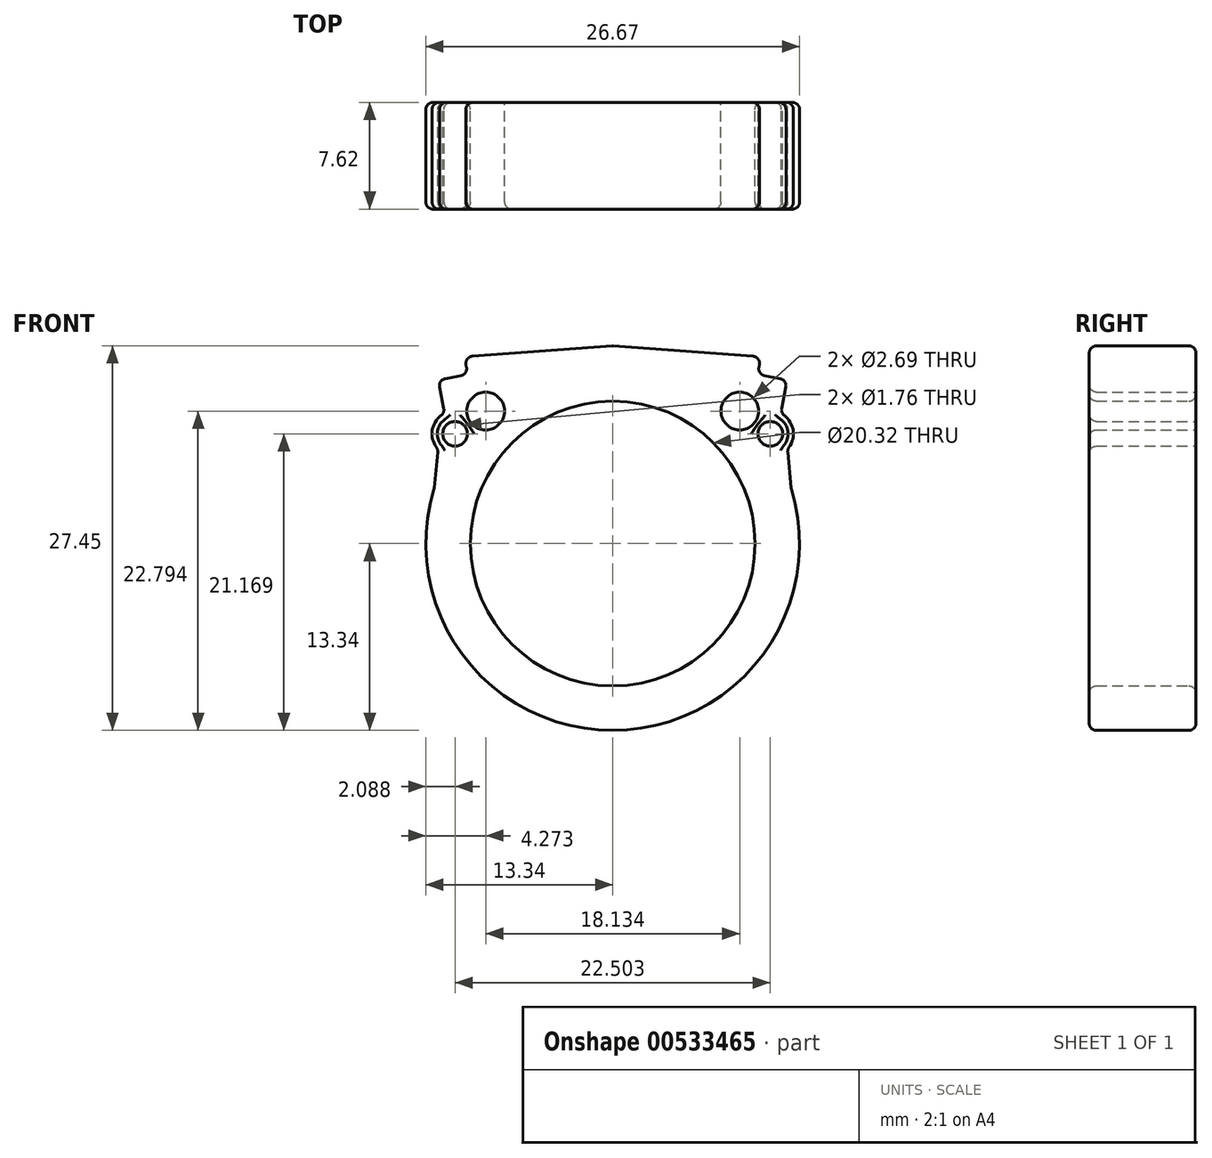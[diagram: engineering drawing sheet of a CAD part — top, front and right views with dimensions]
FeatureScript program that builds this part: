
annotation { "Feature Type Name" : "Feature", "Feature Type Description" : "" }
export const myFeature = defineFeature(function(context is Context, id is Id, definition is map)
    precondition{}
    {
        {
            var Q0;
            Q0=qCreatedBy(makeId("Front.planeOp"),FACE);
            var sketch = newSketch(context, id + "F0", { "sketchPlane" : qUnion([Q0])});
            skCircle(sketch, "E0", {"center": v(0, 0) * mm, "radius": 10.16 * mm});
            skArc(sketch, "E1.0", {"start": v(-12.74, 3.94) * mm, "mid": v(0, -13.34) * mm, "end": v(12.74, 3.94) * mm});
            skLineSegment(sketch, "E2", {"start": v(-11.99, 9.3) * mm, "end": v(-12.45, 11.66) * mm});
            skLineSegment(sketch, "E3", {"start": v(-12.45, 11.66) * mm, "end": v(-10.34, 12.08) * mm});
            skPoint(sketch, "E4.orphan", {"position": v(-10.16, 0) * mm});
            skArc(sketch, "E5", {"start": v(-11.99, 9.3) * mm, "mid": v(-12.88, 8.06) * mm, "end": v(-12.36, 6.62) * mm});
            skLineSegment(sketch, "E6", {"start": v(-10.34, 12.08) * mm, "end": v(-10.58, 13.32) * mm});
            skLineSegment(sketch, "E7", {"start": v(-10.58, 13.32) * mm, "end": v(0, 14.11) * mm});
            skLineSegment(sketch, "E8.MirrorCS", {"start": v(12.5, 6.46) * mm, "end": v(12.36, 6.62) * mm});
            skLineSegment(sketch, "E9.MirrorCS", {"start": v(10.58, 13.32) * mm, "end": v(0, 14.11) * mm});
            skLineSegment(sketch, "E10.MirrorCS", {"start": v(10.34, 12.08) * mm, "end": v(10.58, 13.32) * mm});
            skLineSegment(sketch, "E11.MirrorCS", {"start": v(12.45, 11.66) * mm, "end": v(10.34, 12.08) * mm});
            skArc(sketch, "E12.MirrorCS", {"start": v(11.99, 9.3) * mm, "mid": v(12.88, 8.06) * mm, "end": v(12.36, 6.62) * mm});
            skLineSegment(sketch, "E13.MirrorCS", {"start": v(11.99, 9.3) * mm, "end": v(12.45, 11.66) * mm});
            skPoint(sketch, "E14.start.orphan", {"position": v(-13.37, 5.42) * mm});
            skLineSegment(sketch, "E15", {"start": v(-12.74, 3.94) * mm, "end": v(-12.47, 6.73) * mm});
            skPoint(sketch, "E16.orphan", {"position": v(-12.36, 7.86) * mm});
            skLineSegment(sketch, "E17.MirrorCS", {"start": v(12.74, 3.94) * mm, "end": v(12.47, 6.73) * mm});
            skPoint(sketch, "E18.MirrorCS.end.orphan", {"position": v(13.37, 5.42) * mm});
            skPoint(sketch, "E18.MirrorCS.start.orphan", {"position": v(12.74, 3.94) * mm});
            skSolve(sketch);
        }
        {
            var Q0;
            Q0 = qSketchRegion(id + "F0", true);
            extrude(context, id + "F1", {"entities" : qUnion([Q0]), "depth" : 7.62 * mm, "offsetDistance" : 25.4 * mm});
        }
        {
            var Q0;
            Q0=makeQuery(id+"F1.opExtrude","CAP_FACE",FACE,{"disambiguationData":[OSD([sQuery(id+"F0.wireOp",EDGE,"E0"),sQuery(id+"F0.wireOp",EDGE,"E1.0"),sQuery(id+"F0.wireOp",EDGE,"E2"),sQuery(id+"F0.wireOp",EDGE,"E3"),sQuery(id+"F0.wireOp",EDGE,"E5"),sQuery(id+"F0.wireOp",EDGE,"E6"),sQuery(id+"F0.wireOp",EDGE,"E7"),sQuery(id+"F0.wireOp",EDGE,"E9.MirrorCS"),sQuery(id+"F0.wireOp",EDGE,"E10.MirrorCS"),sQuery(id+"F0.wireOp",EDGE,"E11.MirrorCS"),sQuery(id+"F0.wireOp",EDGE,"E12.MirrorCS"),sQuery(id+"F0.wireOp",EDGE,"E13.MirrorCS"),sQuery(id+"F0.wireOp",EDGE,"E15"),sQuery(id+"F0.wireOp",EDGE,"E17.MirrorCS")])],"isStart":true});
            var sketch = newSketch(context, id + "F2", { "sketchPlane" : qUnion([Q0])});
            skCircle(sketch, "E19", {"center": v(-9.07, 9.45) * mm, "radius": 1.34 * mm});
            skCircle(sketch, "E20", {"center": v(-11.25, 7.83) * mm, "radius": 0.88 * mm});
            skCircle(sketch, "E21.MirrorC", {"center": v(9.07, 9.45) * mm, "radius": 1.34 * mm});
            skCircle(sketch, "E22.MirrorC", {"center": v(11.25, 7.83) * mm, "radius": 0.88 * mm});
            skSolve(sketch);
        }
        {
            var Q0;
            Q0 = qSketchRegion(id + "F2", true);
            extrude(context, id + "F3", {"entities" : qUnion([Q0]), "operationType" : NewBodyOperationType.REMOVE, "endBound" : BoundingType.THROUGH_ALL, "oppositeDirection" : true, "depth" : 25.4 * mm, "offsetDistance" : 25.4 * mm});
        }
        {
            var Q0;
            Q0=makeQuery(id+"F1.opExtrude","CAP_EDGE",EDGE,{"disambiguationData":[OSD([sQuery(id+"F0.wireOp",EDGE,"E0")])],"isStart":false});
            var Q1;
            Q1=makeQuery(id+"F1.opExtrude","SWEPT_EDGE",EDGE,{"disambiguationData":[OSD([sQuery(id+"F0.wireOp",EDGE,"E1.0"),sQuery(id+"F0.wireOp",EDGE,"E17.MirrorCS")])]});
            var Q2;
            Q2=makeQuery(id+"F1.opExtrude","CAP_EDGE",EDGE,{"disambiguationData":[OSD([sQuery(id+"F0.wireOp",EDGE,"E1.0")])],"isStart":true});
            var Q3;
            Q3=makeQuery(id+"F1.opExtrude","SWEPT_EDGE",EDGE,{"disambiguationData":[OSD([sQuery(id+"F0.wireOp",EDGE,"E10.MirrorCS"),sQuery(id+"F0.wireOp",EDGE,"E11.MirrorCS")])]});
            var Q4;
            Q4=makeQuery(id+"F1.opExtrude","SWEPT_EDGE",EDGE,{"disambiguationData":[OSD([sQuery(id+"F0.wireOp",EDGE,"E9.MirrorCS"),sQuery(id+"F0.wireOp",EDGE,"E10.MirrorCS")])]});
            var Q5;
            Q5=makeQuery(id+"F1.opExtrude","SWEPT_EDGE",EDGE,{"disambiguationData":[OSD([sQuery(id+"F0.wireOp",EDGE,"E12.MirrorCS"),sQuery(id+"F0.wireOp",EDGE,"E13.MirrorCS")])]});
            var Q6;
            Q6=makeQuery(id+"F1.opExtrude","CAP_EDGE",EDGE,{"disambiguationData":[OSD([sQuery(id+"F0.wireOp",EDGE,"E9.MirrorCS")])],"isStart":false});
            var Q7;
            Q7=makeQuery(id+"F1.opExtrude","SWEPT_EDGE",EDGE,{"disambiguationData":[OSD([sQuery(id+"F0.wireOp",EDGE,"E11.MirrorCS"),sQuery(id+"F0.wireOp",EDGE,"E13.MirrorCS")])]});
            var Q8;
            Q8=makeQuery(id+"F1.opExtrude","CAP_EDGE",EDGE,{"disambiguationData":[OSD([sQuery(id+"F0.wireOp",EDGE,"E12.MirrorCS")])],"isStart":true});
            var Q9;
            Q9=makeQuery(id+"F1.opExtrude","CAP_EDGE",EDGE,{"disambiguationData":[OSD([sQuery(id+"F0.wireOp",EDGE,"E1.0")])],"isStart":false});
            var Q10;
            Q10=makeQuery(id+"F1.opExtrude","SWEPT_EDGE",EDGE,{"disambiguationData":[OSD([sQuery(id+"F0.wireOp",EDGE,"E12.MirrorCS"),sQuery(id+"F0.wireOp",EDGE,"E17.MirrorCS")])]});
            var Q11;
            Q11=makeQuery(id+"F1.opExtrude","CAP_EDGE",EDGE,{"disambiguationData":[OSD([sQuery(id+"F0.wireOp",EDGE,"E12.MirrorCS")])],"isStart":false});
            var Q12;
            Q12=makeQuery(id+"F1.opExtrude","CAP_EDGE",EDGE,{"disambiguationData":[OSD([sQuery(id+"F0.wireOp",EDGE,"E10.MirrorCS")])],"isStart":false});
            var Q13;
            Q13=makeQuery(id+"F1.opExtrude","SWEPT_EDGE",EDGE,{"disambiguationData":[OSD([sQuery(id+"F0.wireOp",EDGE,"E6"),sQuery(id+"F0.wireOp",EDGE,"E7")])]});
            var Q14;
            Q14=makeQuery(id+"F1.opExtrude","CAP_EDGE",EDGE,{"disambiguationData":[OSD([sQuery(id+"F0.wireOp",EDGE,"E11.MirrorCS")])],"isStart":true});
            var Q15;
            Q15=makeQuery(id+"F1.opExtrude","CAP_EDGE",EDGE,{"disambiguationData":[OSD([sQuery(id+"F0.wireOp",EDGE,"E7")])],"isStart":false});
            var Q16;
            Q16=makeQuery(id+"F1.opExtrude","CAP_EDGE",EDGE,{"disambiguationData":[OSD([sQuery(id+"F0.wireOp",EDGE,"E17.MirrorCS")])],"isStart":false});
            var Q17;
            Q17=makeQuery(id+"F1.opExtrude","SWEPT_EDGE",EDGE,{"disambiguationData":[OSD([sQuery(id+"F0.wireOp",EDGE,"E3"),sQuery(id+"F0.wireOp",EDGE,"E6")])]});
            var Q18;
            Q18=makeQuery(id+"F1.opExtrude","SWEPT_EDGE",EDGE,{"disambiguationData":[OSD([sQuery(id+"F0.wireOp",EDGE,"E1.0"),sQuery(id+"F0.wireOp",EDGE,"E15")])]});
            var Q19;
            Q19=makeQuery(id+"F1.opExtrude","SWEPT_EDGE",EDGE,{"disambiguationData":[OSD([sQuery(id+"F0.wireOp",EDGE,"E5"),sQuery(id+"F0.wireOp",EDGE,"E15")])]});
            var Q20;
            Q20=makeQuery(id+"F1.opExtrude","CAP_EDGE",EDGE,{"disambiguationData":[OSD([sQuery(id+"F0.wireOp",EDGE,"E11.MirrorCS")])],"isStart":false});
            var Q21;
            Q21=makeQuery(id+"F1.opExtrude","CAP_EDGE",EDGE,{"disambiguationData":[OSD([sQuery(id+"F0.wireOp",EDGE,"E2")])],"isStart":true});
            var Q22;
            Q22=makeQuery(id+"FAl7ck8pDMkB1d6_1.boolean.opBoolean","INTERSECT",EDGE,{"derivedFrom":[makeQuery(id+"F1.opExtrude","SWEPT_FACE",FACE,{"disambiguationData":[OSD([sQuery(id+"F0.wireOp",EDGE,"E7")])]}),makeQuery(id+"FAl7ck8pDMkB1d6_1.opRevolve","SWEPT_FACE",FACE,{"disambiguationData":[OSD([sQuery(id+"FdSJt1zroz8b4NX_1.wireOp",EDGE,"vg2aCjqp-GtUR-O7Jh-xMUV-T6dl1fkwozAl")])]})]});
            var Q23;
            Q23=makeQuery(id+"F1.opExtrude","CAP_EDGE",EDGE,{"disambiguationData":[OSD([sQuery(id+"F0.wireOp",EDGE,"E0")])],"isStart":true});
            var Q24;
            Q24=makeQuery(id+"F1.opExtrude","SWEPT_EDGE",EDGE,{"disambiguationData":[OSD([sQuery(id+"F0.wireOp",EDGE,"E2"),sQuery(id+"F0.wireOp",EDGE,"E5")])]});
            var Q25;
            Q25=makeQuery(id+"F1.opExtrude","CAP_EDGE",EDGE,{"disambiguationData":[OSD([sQuery(id+"F0.wireOp",EDGE,"E10.MirrorCS")])],"isStart":true});
            var Q26;
            Q26=makeQuery(id+"F1.opExtrude","SWEPT_EDGE",EDGE,{"disambiguationData":[OSD([sQuery(id+"F0.wireOp",EDGE,"E2"),sQuery(id+"F0.wireOp",EDGE,"E3")])]});
            var Q27;
            Q27=makeQuery(id+"F1.opExtrude","CAP_EDGE",EDGE,{"disambiguationData":[OSD([sQuery(id+"F0.wireOp",EDGE,"E13.MirrorCS")])],"isStart":true});
            var Q28;
            Q28=makeQuery(id+"F1.opExtrude","CAP_EDGE",EDGE,{"disambiguationData":[OSD([sQuery(id+"F0.wireOp",EDGE,"E3")])],"isStart":false});
            var Q29;
            Q29=makeQuery(id+"F1.opExtrude","CAP_EDGE",EDGE,{"disambiguationData":[OSD([sQuery(id+"F0.wireOp",EDGE,"E5")])],"isStart":true});
            var Q30;
            Q30=makeQuery(id+"F1.opExtrude","CAP_EDGE",EDGE,{"disambiguationData":[OSD([sQuery(id+"F0.wireOp",EDGE,"E13.MirrorCS")])],"isStart":false});
            var Q31;
            Q31=makeQuery(id+"F1.opExtrude","CAP_EDGE",EDGE,{"disambiguationData":[OSD([sQuery(id+"F0.wireOp",EDGE,"E17.MirrorCS")])],"isStart":true});
            var Q32;
            Q32=makeQuery(id+"F1.opExtrude","CAP_EDGE",EDGE,{"disambiguationData":[OSD([sQuery(id+"F0.wireOp",EDGE,"E6")])],"isStart":false});
            var Q33;
            Q33=makeQuery(id+"F1.opExtrude","CAP_EDGE",EDGE,{"disambiguationData":[OSD([sQuery(id+"F0.wireOp",EDGE,"E7")])],"isStart":true});
            var Q34;
            Q34=makeQuery(id+"F1.opExtrude","CAP_EDGE",EDGE,{"disambiguationData":[OSD([sQuery(id+"F0.wireOp",EDGE,"E9.MirrorCS")])],"isStart":true});
            var Q35;
            {var subQ0=sQuery(id+"F0.wireOp",EDGE,"E9.MirrorCS");var subQ1=sQuery(id+"F0.wireOp",EDGE,"E7");Q35=makeQuery(id+"FAl7ck8pDMkB1d6_1.boolean.opBoolean","SPLIT",EDGE,{"disambiguationData":[TD([makeQuery(id+"F1.opExtrude","CAP_FACE",FACE,{"disambiguationData":[OSD([sQuery(id+"F0.wireOp",EDGE,"E0"),sQuery(id+"F0.wireOp",EDGE,"E1.0"),sQuery(id+"F0.wireOp",EDGE,"E2"),sQuery(id+"F0.wireOp",EDGE,"E3"),sQuery(id+"F0.wireOp",EDGE,"E5"),sQuery(id+"F0.wireOp",EDGE,"E6"),subQ1,subQ0,sQuery(id+"F0.wireOp",EDGE,"E10.MirrorCS"),sQuery(id+"F0.wireOp",EDGE,"E11.MirrorCS"),sQuery(id+"F0.wireOp",EDGE,"E12.MirrorCS"),sQuery(id+"F0.wireOp",EDGE,"E13.MirrorCS"),sQuery(id+"F0.wireOp",EDGE,"E15"),sQuery(id+"F0.wireOp",EDGE,"E17.MirrorCS")])],"isStart":false})])],"derivedFrom":makeQuery(id+"F1.opExtrude","SWEPT_EDGE",EDGE,{"disambiguationData":[OSD([subQ1,subQ0])]})});}
            var Q36;
            Q36=makeQuery(id+"FAl7ck8pDMkB1d6_1.boolean.opBoolean","INTERSECT",EDGE,{"derivedFrom":[makeQuery(id+"F1.opExtrude","SWEPT_FACE",FACE,{"disambiguationData":[OSD([sQuery(id+"F0.wireOp",EDGE,"E9.MirrorCS")])]}),makeQuery(id+"FAl7ck8pDMkB1d6_1.opRevolve","SWEPT_FACE",FACE,{"disambiguationData":[OSD([sQuery(id+"FdSJt1zroz8b4NX_1.wireOp",EDGE,"vg2aCjqp-GtUR-O7Jh-xMUV-T6dl1fkwozAl")])]})]});
            var Q37;
            Q37=makeQuery(id+"F1.opExtrude","CAP_EDGE",EDGE,{"disambiguationData":[OSD([sQuery(id+"F0.wireOp",EDGE,"E2")])],"isStart":false});
            var Q38;
            {var subQ0=sQuery(id+"F0.wireOp",EDGE,"E9.MirrorCS");var subQ1=sQuery(id+"F0.wireOp",EDGE,"E7");Q38=makeQuery(id+"FAl7ck8pDMkB1d6_1.boolean.opBoolean","SPLIT",EDGE,{"disambiguationData":[TD([makeQuery(id+"F1.opExtrude","CAP_FACE",FACE,{"disambiguationData":[OSD([sQuery(id+"F0.wireOp",EDGE,"E0"),sQuery(id+"F0.wireOp",EDGE,"E1.0"),sQuery(id+"F0.wireOp",EDGE,"E2"),sQuery(id+"F0.wireOp",EDGE,"E3"),sQuery(id+"F0.wireOp",EDGE,"E5"),sQuery(id+"F0.wireOp",EDGE,"E6"),subQ1,subQ0,sQuery(id+"F0.wireOp",EDGE,"E10.MirrorCS"),sQuery(id+"F0.wireOp",EDGE,"E11.MirrorCS"),sQuery(id+"F0.wireOp",EDGE,"E12.MirrorCS"),sQuery(id+"F0.wireOp",EDGE,"E13.MirrorCS"),sQuery(id+"F0.wireOp",EDGE,"E15"),sQuery(id+"F0.wireOp",EDGE,"E17.MirrorCS")])],"isStart":true})])],"derivedFrom":makeQuery(id+"F1.opExtrude","SWEPT_EDGE",EDGE,{"disambiguationData":[OSD([subQ1,subQ0])]})});}
            var Q39;
            Q39=makeQuery(id+"F1.opExtrude","CAP_EDGE",EDGE,{"disambiguationData":[OSD([sQuery(id+"F0.wireOp",EDGE,"E5")])],"isStart":false});
            var Q40;
            Q40=makeQuery(id+"F1.opExtrude","CAP_EDGE",EDGE,{"disambiguationData":[OSD([sQuery(id+"F0.wireOp",EDGE,"E3")])],"isStart":true});
            var Q41;
            Q41=makeQuery(id+"F1.opExtrude","CAP_EDGE",EDGE,{"disambiguationData":[OSD([sQuery(id+"F0.wireOp",EDGE,"E15")])],"isStart":true});
            var Q42;
            Q42=makeQuery(id+"F1.opExtrude","CAP_EDGE",EDGE,{"disambiguationData":[OSD([sQuery(id+"F0.wireOp",EDGE,"E6")])],"isStart":true});
            var Q43;
            Q43=makeQuery(id+"F1.opExtrude","CAP_EDGE",EDGE,{"disambiguationData":[OSD([sQuery(id+"F0.wireOp",EDGE,"E15")])],"isStart":false});
            var Q44;
            Q44=makeQuery(id+"F3.boolean.opBoolean","COPY",EDGE,{"derivedFrom":makeQuery(id+"F3.opExtrude","CAP_EDGE",EDGE,{"disambiguationData":[OSD([sQuery(id+"F2.wireOp",EDGE,"E19")])],"isStart":true})});
            var Q45;
            Q45=makeQuery(id+"F3.boolean.opBoolean","COPY",EDGE,{"derivedFrom":makeQuery(id+"F3.opExtrude","CAP_EDGE",EDGE,{"disambiguationData":[OSD([sQuery(id+"F2.wireOp",EDGE,"E20")])],"isStart":true})});
            var Q46;
            Q46=makeQuery(id+"F3.boolean.opBoolean","COPY",EDGE,{"derivedFrom":makeQuery(id+"F3.opExtrude","CAP_EDGE",EDGE,{"disambiguationData":[OSD([sQuery(id+"F2.wireOp",EDGE,"E21.MirrorC")])],"isStart":true})});
            var Q47;
            Q47=makeQuery(id+"F3.boolean.opBoolean","COPY",EDGE,{"derivedFrom":makeQuery(id+"F3.opExtrude","CAP_EDGE",EDGE,{"disambiguationData":[OSD([sQuery(id+"F2.wireOp",EDGE,"E22.MirrorC")])],"isStart":true})});
            var Q48;
            Q48=makeQuery(id+"F3.boolean.opBoolean","INTERSECT",EDGE,{"derivedFrom":[makeQuery(id+"F1.opExtrude","CAP_FACE",FACE,{"disambiguationData":[OSD([sQuery(id+"F0.wireOp",EDGE,"E0"),sQuery(id+"F0.wireOp",EDGE,"E1.0"),sQuery(id+"F0.wireOp",EDGE,"E2"),sQuery(id+"F0.wireOp",EDGE,"E3"),sQuery(id+"F0.wireOp",EDGE,"E5"),sQuery(id+"F0.wireOp",EDGE,"E6"),sQuery(id+"F0.wireOp",EDGE,"E7"),sQuery(id+"F0.wireOp",EDGE,"E9.MirrorCS"),sQuery(id+"F0.wireOp",EDGE,"E10.MirrorCS"),sQuery(id+"F0.wireOp",EDGE,"E11.MirrorCS"),sQuery(id+"F0.wireOp",EDGE,"E12.MirrorCS"),sQuery(id+"F0.wireOp",EDGE,"E13.MirrorCS"),sQuery(id+"F0.wireOp",EDGE,"E15"),sQuery(id+"F0.wireOp",EDGE,"E17.MirrorCS")])],"isStart":false}),makeQuery(id+"F3.opExtrude","SWEPT_FACE",FACE,{"disambiguationData":[OSD([sQuery(id+"F2.wireOp",EDGE,"E21.MirrorC")])]})]});
            var Q49;
            Q49=makeQuery(id+"F3.boolean.opBoolean","INTERSECT",EDGE,{"derivedFrom":[makeQuery(id+"F1.opExtrude","CAP_FACE",FACE,{"disambiguationData":[OSD([sQuery(id+"F0.wireOp",EDGE,"E0"),sQuery(id+"F0.wireOp",EDGE,"E1.0"),sQuery(id+"F0.wireOp",EDGE,"E2"),sQuery(id+"F0.wireOp",EDGE,"E3"),sQuery(id+"F0.wireOp",EDGE,"E5"),sQuery(id+"F0.wireOp",EDGE,"E6"),sQuery(id+"F0.wireOp",EDGE,"E7"),sQuery(id+"F0.wireOp",EDGE,"E9.MirrorCS"),sQuery(id+"F0.wireOp",EDGE,"E10.MirrorCS"),sQuery(id+"F0.wireOp",EDGE,"E11.MirrorCS"),sQuery(id+"F0.wireOp",EDGE,"E12.MirrorCS"),sQuery(id+"F0.wireOp",EDGE,"E13.MirrorCS"),sQuery(id+"F0.wireOp",EDGE,"E15"),sQuery(id+"F0.wireOp",EDGE,"E17.MirrorCS")])],"isStart":false}),makeQuery(id+"F3.opExtrude","SWEPT_FACE",FACE,{"disambiguationData":[OSD([sQuery(id+"F2.wireOp",EDGE,"E22.MirrorC")])]})]});
            var Q50;
            Q50=makeQuery(id+"F3.boolean.opBoolean","INTERSECT",EDGE,{"derivedFrom":[makeQuery(id+"F1.opExtrude","CAP_FACE",FACE,{"disambiguationData":[OSD([sQuery(id+"F0.wireOp",EDGE,"E0"),sQuery(id+"F0.wireOp",EDGE,"E1.0"),sQuery(id+"F0.wireOp",EDGE,"E2"),sQuery(id+"F0.wireOp",EDGE,"E3"),sQuery(id+"F0.wireOp",EDGE,"E5"),sQuery(id+"F0.wireOp",EDGE,"E6"),sQuery(id+"F0.wireOp",EDGE,"E7"),sQuery(id+"F0.wireOp",EDGE,"E9.MirrorCS"),sQuery(id+"F0.wireOp",EDGE,"E10.MirrorCS"),sQuery(id+"F0.wireOp",EDGE,"E11.MirrorCS"),sQuery(id+"F0.wireOp",EDGE,"E12.MirrorCS"),sQuery(id+"F0.wireOp",EDGE,"E13.MirrorCS"),sQuery(id+"F0.wireOp",EDGE,"E15"),sQuery(id+"F0.wireOp",EDGE,"E17.MirrorCS")])],"isStart":false}),makeQuery(id+"F3.opExtrude","SWEPT_FACE",FACE,{"disambiguationData":[OSD([sQuery(id+"F2.wireOp",EDGE,"E19")])]})]});
            var Q51;
            Q51=makeQuery(id+"F3.boolean.opBoolean","INTERSECT",EDGE,{"derivedFrom":[makeQuery(id+"F1.opExtrude","CAP_FACE",FACE,{"disambiguationData":[OSD([sQuery(id+"F0.wireOp",EDGE,"E0"),sQuery(id+"F0.wireOp",EDGE,"E1.0"),sQuery(id+"F0.wireOp",EDGE,"E2"),sQuery(id+"F0.wireOp",EDGE,"E3"),sQuery(id+"F0.wireOp",EDGE,"E5"),sQuery(id+"F0.wireOp",EDGE,"E6"),sQuery(id+"F0.wireOp",EDGE,"E7"),sQuery(id+"F0.wireOp",EDGE,"E9.MirrorCS"),sQuery(id+"F0.wireOp",EDGE,"E10.MirrorCS"),sQuery(id+"F0.wireOp",EDGE,"E11.MirrorCS"),sQuery(id+"F0.wireOp",EDGE,"E12.MirrorCS"),sQuery(id+"F0.wireOp",EDGE,"E13.MirrorCS"),sQuery(id+"F0.wireOp",EDGE,"E15"),sQuery(id+"F0.wireOp",EDGE,"E17.MirrorCS")])],"isStart":false}),makeQuery(id+"F3.opExtrude","SWEPT_FACE",FACE,{"disambiguationData":[OSD([sQuery(id+"F2.wireOp",EDGE,"E20")])]})]});
            fillet(context, id + "F4", {"entities" : qUnion([Q0, Q1, Q2, Q3, Q4, Q5, Q6, Q7, Q8, Q9, Q10, Q11, Q12, Q13, Q14, Q15, Q16, Q17, Q18, Q19, Q20, Q21, Q22, Q23, Q24, Q25, Q26, Q27, Q28, Q29, Q30, Q31, Q32, Q33, Q34, Q35, Q36, Q37, Q38, Q39, Q40, Q41, Q42, Q43, Q44, Q45, Q46, Q47, Q48, Q49, Q50, Q51]), "radius" : 0.5 * mm, "tangentPropagation" : true, "allowEdgeOverflow" : false});
        }
    });
